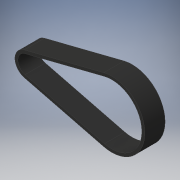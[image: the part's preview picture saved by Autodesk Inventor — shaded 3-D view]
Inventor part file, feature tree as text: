
AUTODESK INVENTOR PART (.ipt)
format: ipt  version: 2019.3 (Build 233278000, 278)  size: 121,344 bytes
history: native  units: mm
features: extrude x1, sketch x1
ambient origin geometry x8: Origin, YZ Plane, XZ Plane, XY Plane, X Axis, Y Axis, Z Axis, Center Point
bodies: Solid1 (feature_tree)
feature tree (2):
  extrude  "Extrusion1"  Depth=62.5mm
  sketch  "Sketch1"  dims[d0=15.28mm d1=62.5mm d3=1.5mm d4=45.84mm d5=0.7mm d6=0.7mm d7=1.5mm d8=15.0mm d9=0.0mm]
